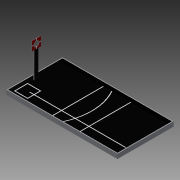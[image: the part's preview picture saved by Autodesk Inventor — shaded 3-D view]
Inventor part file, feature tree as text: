
AUTODESK INVENTOR PART (.ipt)
format: ipt  version: 2014 SP1 (Build 180222100, 222)  size: 524,800 bytes
history: native  units: in
note: dims shown in document units (in); Inventor stores cm internally (conversion verified against a paired STEP export)
features: extrude x10, sketch x10, projected_geometry x6
ambient origin geometry x8: Origin, YZ Plane, XZ Plane, XY Plane, X Axis, Y Axis, Z Axis, Center Point
bodies: Solid1 (feature_tree)
feature tree (26):
  extrude  "Extrusion1"  Depth=49.0in
  extrude  "Extrusion2"  Depth=0.75in
  extrude  "Extrusion3"  Depth=0.75in
  extrude  "Extrusion4"  Depth=3.5in TaperAngle=0.0deg
  extrude  "Extrusion5"  Depth=12.0in
  extrude  "Extrusion6"  Depth=0.75in
  extrude  "Extrusion7"  Depth=10.5in
  extrude  "Extrusion8"  Depth=10.5in
  extrude  "Extrusion9"  Depth=0.75in
  extrude  "Extrusion10"  Depth=0.75in
  sketch  "Sketch1"  dims[d0=97.0in d1=49.0in]
  sketch  "Sketch2"  dims[d2=0.5in d3=0.0in d4=0.75in]
  sketch  "Sketch3"  dims[d5=0.75in d6=0.75in]
  projected_geometry  "Projected Loop1"
  sketch  "Sketch4"  dims[d7=0.75in d8=3.5in d9=0.0in]
  sketch  "Sketch5"  dims[d10=5.0in d11=12.0in]
  projected_geometry  "Projected Loop2"
  projected_geometry  "Projected Loop3"
  projected_geometry  "Projected Loop4"
  projected_geometry  "Projected Loop5"
  sketch  "Sketch6"  dims[d12=12.0in d13=0.75in]
  projected_geometry  "Projected Loop6"
  sketch  "Sketch7"  dims[d14=0.75in d15=10.5in]
  sketch  "Sketch8"  dims[d16=10.5in d17=0.375in]
  sketch  "Sketch9"  dims[d18=84.0in d19=0.75in]
  sketch  "Sketch10"  dims[d20=24.0in d21=0.75in d22=24.0in d23=0.75in d24=11.625in d25=23.75in d26=1.75in d27=3.5in d28=0.75in d29=96.962in d30=97.712in d31=96.212in d32=0.0625in d33=0.0in d38=6.0in d41=2.0in d42=0.25in d43=5.5118in d45=2.0in d46=0.3937in d48=1.0in d50=0.25in d51=5.5118in d53=2.0in d54=0.3937in d56=1.0in d58=0.375in d59=1.0in d60=1.0in d61=0.0in d62=96.962in d63=6.0in d64=1.0in d65=1.0in d67=0.25in d68=8.0in d69=1.0in d70=1.0in d71=2.0in d72=1.0in d73=1.0in d74=2.0in d75=2.0in d76=2.0in d77=2.0in d78=2.0in d79=2.0in d80=2.0in d81=2.0in d82=2.0in d83=2.0in d84=2.0in d85=1.0in d86=1.0in d87=1.0in d88=1.0in d89=1.0in d90=1.0in d91=1.0in d92=1.0in d93=1.0in d94=1.0in d95=1.0in d96=1.0in d97=1.0in d98=1.0in d99=1.0in d100=1.0in d101=1.0in d102=1.0in d103=1.0in d104=1.0in d105=1.0in d106=1.0in d107=0.25in d108=0.25in d109=0.25in d110=0.25in d111=0.25in d112=0.25in d113=0.25in d114=0.25in d115=0.25in d116=0.25in d117=0.25in d118=0.25in d119=0.25in d120=0.25in d121=0.25in d122=0.25in d123=0.25in d124=0.25in d125=0.25in d126=0.25in d127=0.25in d128=0.25in d129=0.25in d130=0.25in d131=0.25in d132=0.25in d133=0.25in d134=1.0in d135=0.0in d136=0.375in d137=6.0in d138=1.0in d139=1.0in d140=0.25in d141=0.25in d142=5.5118in d144=2.0in d145=0.3937in d147=1.0in d149=1.0in d150=0.0in d151=23.9375in d152=0.0in d153=1.0in d154=4.0in d155=8.0in d156=8.0in d157=0.25in d158=0.0in d160=0.375in d161=0.75in d162=0.375in d163=0.75in d164=0.0625in d165=0.0in d166=5.0in d167=1.0in d168=0.0in]
